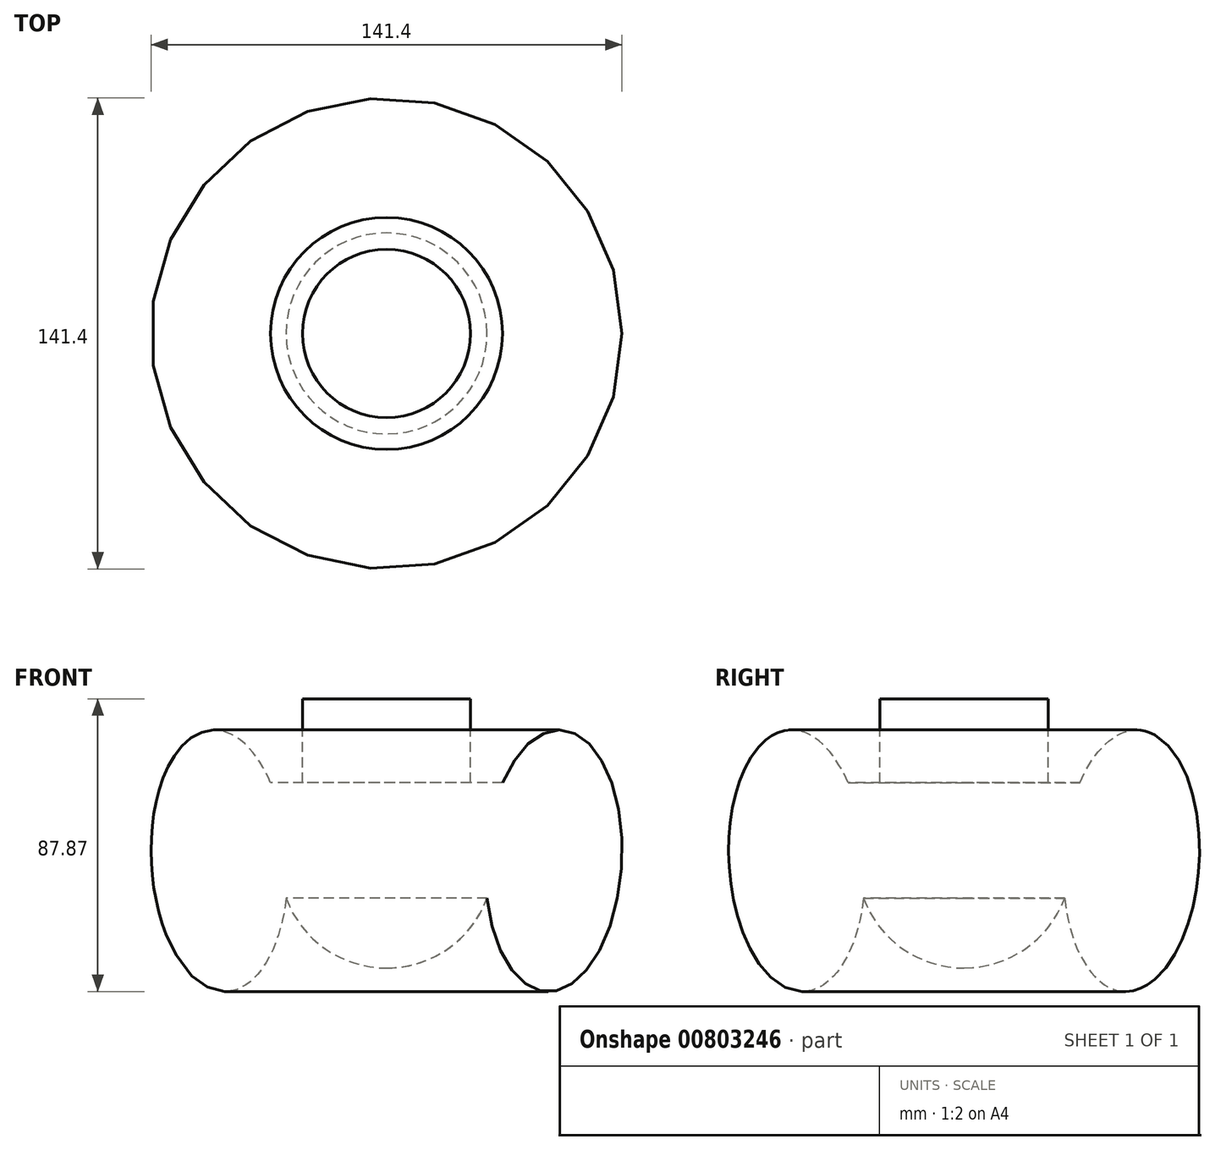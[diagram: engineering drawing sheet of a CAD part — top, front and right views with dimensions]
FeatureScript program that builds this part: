
annotation { "Feature Type Name" : "Feature", "Feature Type Description" : "" }
export const myFeature = defineFeature(function(context is Context, id is Id, definition is map)
    precondition{}
    {
        {
            var Q0;
            Q0=qCreatedBy(makeId("Front.planeOp"),FACE);
            var sketch = newSketch(context, id + "F0", { "sketchPlane" : qUnion([Q0])});
            skLineSegment(sketch, "E0", {"start": v(0, 78.47) * mm, "end": v(0, -77.15) * mm, "construction": true});
            skLineSegment(sketch, "E1.top", {"start": v(0, 48.62) * mm, "end": v(25.25, 48.62) * mm});
            skLineSegment(sketch, "E1.right", {"start": v(25.25, 23.47) * mm, "end": v(25.25, 48.62) * mm});
            skLineSegment(sketch, "E2.top", {"start": v(25.25, 23.47) * mm, "end": v(34.83, 23.47) * mm});
            skArc(sketch, "E3", {"start": v(0, -32.22) * mm, "mid": v(18.37, -26.47) * mm, "end": v(30.18, -11.27) * mm});
            skEllipticalArc(sketch, "E4", {});
            skLineSegment(sketch, "E5", {"start": v(0, 48.62) * mm, "end": v(0, -32.22) * mm});
            const initialGuessF0  = {"E4": [0.050216034054756165, 0, -0.057321890195519025, -0.99835574867099, 0.03929882695417494, 0.020395859138649556, 5.0334260376456506, 4.101399066528838]};
            skSetInitialGuess(sketch, initialGuessF0);
            skSolve(sketch);
        }
        {
            var Q0;
            Q0=makeQuery(id+"F0.imprint","IMPRINT",FACE,{"disambiguationData":[TD([[makeQuery(id+"F0.imprint","IMPRINT",EDGE,{"derivedFrom":sQuery(id+"F0.wireOp",EDGE,"E1.top")}),-1.0]])]});
            var Q1;
            Q1=sQuery(id+"F0.wireOp",EDGE,"E0");
            revolve(context, id + "F1", {"surfaceOperationType" : NewSurfaceOperationType.NEW, "entities" : qUnion([Q0]), "axis" : qUnion([Q1]), "revolveType" : RevolveType.FULL});
        }
    });
